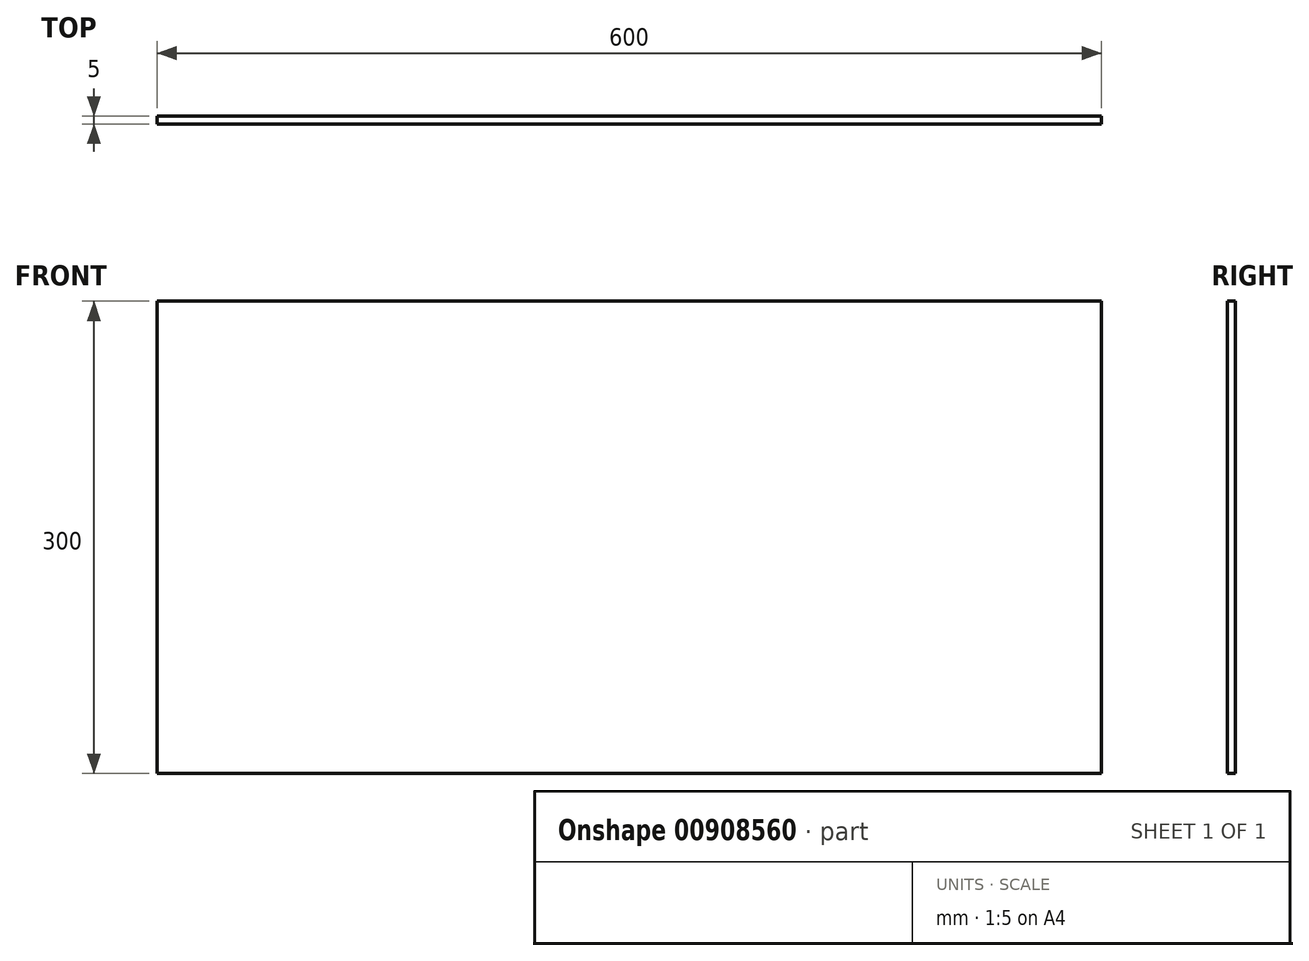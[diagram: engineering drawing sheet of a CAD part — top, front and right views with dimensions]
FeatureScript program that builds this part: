
annotation { "Feature Type Name" : "Feature", "Feature Type Description" : "" }
export const myFeature = defineFeature(function(context is Context, id is Id, definition is map)
    precondition{}
    {
        {
            var Q0;
            Q0=qCreatedBy(makeId("Front.planeOp"),FACE);
            var sketch = newSketch(context, id + "F0", { "sketchPlane" : qUnion([Q0])});
            skLineSegment(sketch, "E0.bottom", {"start": v(300, -150) * mm, "end": v(-300, -150) * mm});
            skLineSegment(sketch, "E0.top", {"start": v(300, 150) * mm, "end": v(-300, 150) * mm});
            skLineSegment(sketch, "E0.left", {"start": v(300, -150) * mm, "end": v(300, 150) * mm});
            skLineSegment(sketch, "E0.right", {"start": v(-300, -150) * mm, "end": v(-300, 150) * mm});
            skPoint(sketch, "E0.middle", {"position": v(0, 0) * mm});
            skSolve(sketch);
        }
        {
            var Q0;
            Q0=makeQuery(id+"F0.imprint","IMPRINT",FACE,{"disambiguationData":[TD([[makeQuery(id+"F0.imprint","IMPRINT",EDGE,{"derivedFrom":sQuery(id+"F0.wireOp",EDGE,"E0.bottom")}),-1.0]])]});
            extrude(context, id + "F1", {"entities" : qUnion([Q0]), "depth" : 5 * mm, "offsetDistance" : 25 * mm});
        }
    });
